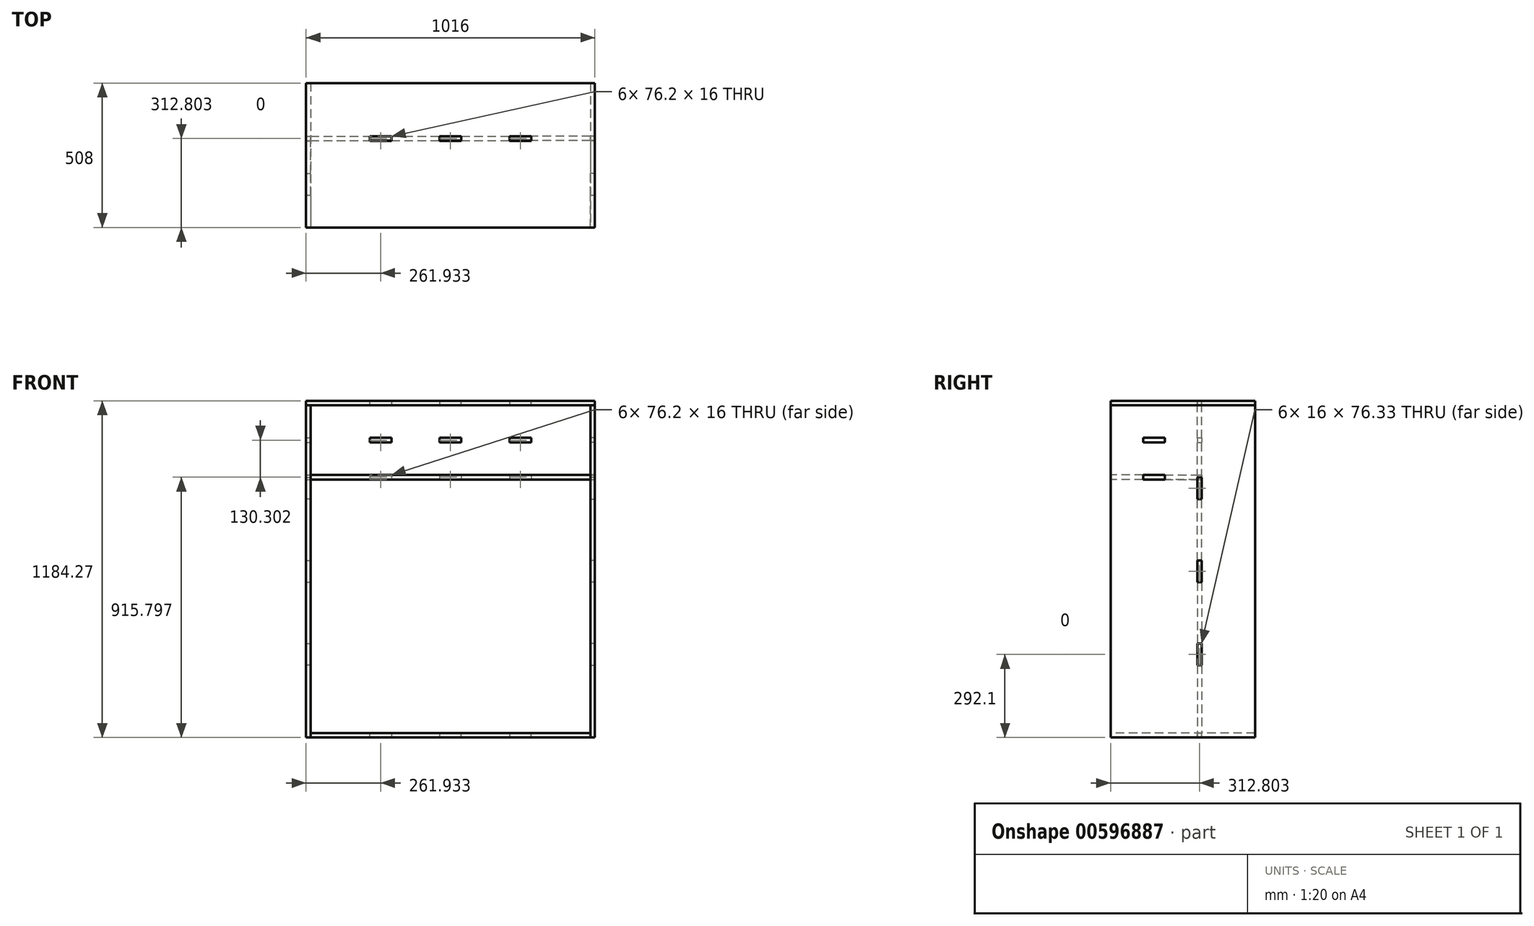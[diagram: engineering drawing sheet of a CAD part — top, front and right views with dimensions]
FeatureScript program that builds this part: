
annotation { "Feature Type Name" : "Feature", "Feature Type Description" : "" }
export const myFeature = defineFeature(function(context is Context, id is Id, definition is map)
    precondition{}
    {
        {
            var Q0;
            Q0=qCreatedBy(makeId("Top.planeOp"),FACE);
            var sketch = newSketch(context, id + "F0", { "sketchPlane" : qUnion([Q0])});
            skLineSegment(sketch, "E0.bottom", {"start": v(-880.8, 468.9) * mm, "end": v(103.44, 468.9) * mm});
            skLineSegment(sketch, "E0.top", {"start": v(-880.8, -39.1) * mm, "end": v(103.44, -39.1) * mm});
            skLineSegment(sketch, "E0.left", {"start": v(-880.8, 468.9) * mm, "end": v(-880.8, -39.1) * mm});
            skLineSegment(sketch, "E0.right", {"start": v(103.44, 468.9) * mm, "end": v(103.44, -39.1) * mm});
            skLineSegment(sketch, "E1", {"start": v(-880.8, 265.7) * mm, "end": v(103.44, 265.7) * mm, "construction": true});
            skLineSegment(sketch, "E2", {"start": v(-388.68, 468.9) * mm, "end": v(-388.68, -39.1) * mm, "construction": true});
            skPoint(sketch, "E3", {"position": v(-634.75, 468.9) * mm});
            skPoint(sketch, "E4", {"position": v(-142.62, 468.9) * mm});
            skLineSegment(sketch, "E5", {"start": v(-634.75, 468.9) * mm, "end": v(-634.75, -39.1) * mm, "construction": true});
            skLineSegment(sketch, "E6", {"start": v(-142.62, 468.9) * mm, "end": v(-142.62, -39.1) * mm, "construction": true});
            skLineSegment(sketch, "E7.bottom", {"start": v(-672.85, 265.7) * mm, "end": v(-596.65, 265.7) * mm});
            skLineSegment(sketch, "E7.top", {"start": v(-672.85, 281.7) * mm, "end": v(-596.65, 281.7) * mm});
            skLineSegment(sketch, "E7.left", {"start": v(-672.85, 265.7) * mm, "end": v(-672.85, 281.7) * mm});
            skLineSegment(sketch, "E7.right", {"start": v(-596.65, 265.7) * mm, "end": v(-596.65, 281.7) * mm});
            skPoint(sketch, "E8", {"position": v(-634.75, 281.7) * mm});
            skLineSegment(sketch, "E9.bottom", {"start": v(-426.78, 265.7) * mm, "end": v(-350.58, 265.7) * mm});
            skLineSegment(sketch, "E9.top", {"start": v(-426.78, 281.7) * mm, "end": v(-350.58, 281.7) * mm});
            skLineSegment(sketch, "E9.left", {"start": v(-426.78, 265.7) * mm, "end": v(-426.78, 281.7) * mm});
            skLineSegment(sketch, "E9.right", {"start": v(-350.58, 265.7) * mm, "end": v(-350.58, 281.7) * mm});
            skLineSegment(sketch, "E10.bottom", {"start": v(-180.72, 265.7) * mm, "end": v(-104.52, 265.7) * mm});
            skLineSegment(sketch, "E10.top", {"start": v(-180.72, 281.7) * mm, "end": v(-104.52, 281.7) * mm});
            skLineSegment(sketch, "E10.left", {"start": v(-180.72, 265.7) * mm, "end": v(-180.72, 281.7) * mm});
            skLineSegment(sketch, "E10.right", {"start": v(-104.52, 265.7) * mm, "end": v(-104.52, 281.7) * mm});
            skPoint(sketch, "E11", {"position": v(-388.68, 281.7) * mm});
            skPoint(sketch, "E12", {"position": v(-142.62, 281.7) * mm});
            skSolve(sketch);
        }
        {
            var Q0;
            Q0=makeQuery(id+"F0.imprint","IMPRINT",FACE,{"disambiguationData":[TD([[makeQuery(id+"F0.imprint","IMPRINT",EDGE,{"derivedFrom":sQuery(id+"F0.wireOp",EDGE,"E0.bottom")}),-1.0]])]});
            extrude(context, id + "F1", {"entities" : qUnion([Q0]), "depth" : 15.88 * mm, "offsetDistance" : 25.4 * mm});
        }
        {
            var Q0;
            Q0=makeQuery(id+"F1.opExtrude","SWEPT_FACE",FACE,{"disambiguationData":[OSD([sQuery(id+"F0.wireOp",EDGE,"E0.left")])]});
            var sketch = newSketch(context, id + "F2", { "sketchPlane" : qUnion([Q0])});
            skLineSegment(sketch, "E13.bottom", {"start": v(-468.9, 0) * mm, "end": v(39.1, 0) * mm});
            skLineSegment(sketch, "E13.top", {"start": v(-468.9, 1168.4) * mm, "end": v(39.1, 1168.4) * mm});
            skLineSegment(sketch, "E13.left", {"start": v(-468.9, 0) * mm, "end": v(-468.9, 1168.4) * mm});
            skLineSegment(sketch, "E13.right", {"start": v(39.1, 0) * mm, "end": v(39.1, 1168.4) * mm});
            skLineSegment(sketch, "E14", {"start": v(-468.9, 584.2) * mm, "end": v(39.1, 584.2) * mm, "construction": true});
            skLineSegment(sketch, "E15", {"start": v(-468.9, 876.3) * mm, "end": v(39.1, 876.3) * mm, "construction": true});
            skLineSegment(sketch, "E16", {"start": v(-468.9, 292.1) * mm, "end": v(39.1, 292.1) * mm, "construction": true});
            skLineSegment(sketch, "E17", {"start": v(-265.7, 1168.4) * mm, "end": v(-265.7, 0) * mm, "construction": true});
            skLineSegment(sketch, "E18.bottom", {"start": v(-265.7, 914.46) * mm, "end": v(-281.7, 914.46) * mm});
            skLineSegment(sketch, "E18.top", {"start": v(-265.7, 838.14) * mm, "end": v(-281.7, 838.14) * mm});
            skLineSegment(sketch, "E18.left", {"start": v(-265.7, 914.46) * mm, "end": v(-265.7, 838.14) * mm});
            skLineSegment(sketch, "E18.right", {"start": v(-281.7, 914.46) * mm, "end": v(-281.7, 838.14) * mm});
            skLineSegment(sketch, "E19.bottom", {"start": v(-265.7, 622.36) * mm, "end": v(-281.7, 622.36) * mm});
            skLineSegment(sketch, "E19.top", {"start": v(-265.7, 546.04) * mm, "end": v(-281.7, 546.04) * mm});
            skLineSegment(sketch, "E19.left", {"start": v(-265.7, 622.36) * mm, "end": v(-265.7, 546.04) * mm});
            skLineSegment(sketch, "E19.right", {"start": v(-281.7, 622.36) * mm, "end": v(-281.7, 546.04) * mm});
            skLineSegment(sketch, "E20.bottom", {"start": v(-265.7, 253.94) * mm, "end": v(-281.7, 253.94) * mm});
            skLineSegment(sketch, "E20.top", {"start": v(-265.7, 330.26) * mm, "end": v(-281.7, 330.26) * mm});
            skLineSegment(sketch, "E20.left", {"start": v(-265.7, 253.94) * mm, "end": v(-265.7, 330.26) * mm});
            skLineSegment(sketch, "E20.right", {"start": v(-281.7, 253.94) * mm, "end": v(-281.7, 330.26) * mm});
            skPoint(sketch, "E21", {"position": v(-281.7, 876.3) * mm});
            skPoint(sketch, "E22", {"position": v(-281.7, 584.2) * mm});
            skPoint(sketch, "E23", {"position": v(-281.7, 292.1) * mm});
            skLineSegment(sketch, "E24", {"start": v(39.1, 1054.1) * mm, "end": v(-468.9, 1054.1) * mm, "construction": true});
            skLineSegment(sketch, "E25", {"start": v(-113.3, 1168.4) * mm, "end": v(-113.3, 1054.1) * mm, "construction": true});
            skLineSegment(sketch, "E26.bottom", {"start": v(-75.14, 1054.1) * mm, "end": v(-151.46, 1054.1) * mm});
            skLineSegment(sketch, "E26.top", {"start": v(-75.14, 1038.1) * mm, "end": v(-151.46, 1038.1) * mm});
            skLineSegment(sketch, "E26.left", {"start": v(-75.14, 1054.1) * mm, "end": v(-75.14, 1038.1) * mm});
            skLineSegment(sketch, "E26.right", {"start": v(-151.46, 1054.1) * mm, "end": v(-151.46, 1038.1) * mm});
            skPoint(sketch, "E27", {"position": v(-113.3, 1054.1) * mm});
            skLineSegment(sketch, "E28", {"start": v(39.1, 923.8) * mm, "end": v(-265.7, 923.8) * mm, "construction": true});
            skPoint(sketch, "E29.oppositeSnap0", {"position": v(-151.46, 1046.1) * mm});
            skLineSegment(sketch, "E29.bottom", {"start": v(-75.14, 923.8) * mm, "end": v(-151.46, 923.8) * mm});
            skLineSegment(sketch, "E29.top", {"start": v(-75.14, 907.8) * mm, "end": v(-151.46, 907.8) * mm});
            skLineSegment(sketch, "E29.left", {"start": v(-75.14, 923.8) * mm, "end": v(-75.14, 907.8) * mm});
            skLineSegment(sketch, "E29.right", {"start": v(-151.46, 923.8) * mm, "end": v(-151.46, 907.8) * mm});
            skSolve(sketch);
        }
        {
            var Q0;
            {var subQ0=sQuery(id+"F2.wireOp",EDGE,"E13.top");Q0=makeQuery(id+"F2.imprint","IMPRINT",FACE,{"disambiguationData":[TD([[makeQuery(id+"F2.imprint","IMPRINT",EDGE,{"derivedFrom":subQ0}),-1.0]])]});}
            var Q1;
            {var subQ0=sQuery(id+"F2.wireOp",EDGE,"E13.bottom");Q1=makeQuery(id+"F2.imprint","IMPRINT",FACE,{"disambiguationData":[TD([[makeQuery(id+"F2.imprint","IMPRINT",EDGE,{"derivedFrom":subQ0}),1.0]])]});}
            extrude(context, id + "F3", {"entities" : qUnion([Q0, Q1]), "depth" : 15.88 * mm, "offsetDistance" : 25.4 * mm});
        }
        {
            var Q0;
            Q0=makeQuery(id+"F1.opExtrude","CAP_EDGE",EDGE,{"disambiguationData":[OSD([sQuery(id+"F0.wireOp",EDGE,"E0.top")])],"isStart":false});
            cPoint(context, id + "F4", {"entities" : qUnion([Q0]), "parameter" : 0.5});
        }
        {
            var Q0;
            Q0=makeQuery(id+"F1.opExtrude","CAP_EDGE",EDGE,{"disambiguationData":[OSD([sQuery(id+"F0.wireOp",EDGE,"E0.bottom")])],"isStart":false});
            cPoint(context, id + "F5", {"entities" : qUnion([Q0]), "parameter" : 0.5});
        }
        {
            var Q0;
            Q0=makeQuery(id+"F1.opExtrude","CAP_EDGE",EDGE,{"disambiguationData":[OSD([sQuery(id+"F0.wireOp",EDGE,"E0.top")])],"isStart":true});
            cPoint(context, id + "F6", {"entities" : qUnion([Q0]), "parameter" : 0.5});
        }
        {
            var Q0;
            Q0 = qCreatedBy(id + "F4" ,VERTEX);
            var Q1;
            Q1 = qCreatedBy(id + "F5" ,VERTEX);
            var Q2;
            Q2 = qCreatedBy(id + "F6" ,VERTEX);
            cPlane(context, id + "F7", {"entities" : qUnion([Q0, Q1, Q2]), "cplaneType" : CPlaneType.THREE_POINT, "offset" : 25.4 * mm, "width" : 152.4 * mm, "height" : 152.4 * mm});
        }
        {
            var Q0;
            Q0=makeQuery(id+"F3.opExtrude","SWEPT_BODY",BODY,{"disambiguationData":[OSD([sQuery(id+"F2.wireOp",EDGE,"E13.bottom"),sQuery(id+"F2.wireOp",EDGE,"E13.top"),sQuery(id+"F2.wireOp",EDGE,"E13.left"),sQuery(id+"F2.wireOp",EDGE,"E13.right"),sQuery(id+"F2.wireOp",EDGE,"E18.bottom"),sQuery(id+"F2.wireOp",EDGE,"E18.top"),sQuery(id+"F2.wireOp",EDGE,"E18.left"),sQuery(id+"F2.wireOp",EDGE,"E18.right"),sQuery(id+"F2.wireOp",EDGE,"E19.bottom"),sQuery(id+"F2.wireOp",EDGE,"E19.top"),sQuery(id+"F2.wireOp",EDGE,"E19.left"),sQuery(id+"F2.wireOp",EDGE,"E19.right"),sQuery(id+"F2.wireOp",EDGE,"E20.bottom"),sQuery(id+"F2.wireOp",EDGE,"E20.top"),sQuery(id+"F2.wireOp",EDGE,"E20.left"),sQuery(id+"F2.wireOp",EDGE,"E20.right")])]});
            var Q1;
            Q1=qCreatedBy(id+"F7.planeOp",FACE);
            mirror(context, id + "F8", {"entities" : qUnion([Q0]), "mirrorPlane" : qUnion([Q1])});
        }
        {
            var Q0;
            Q0=makeQuery(id+"F3.opExtrude","SWEPT_FACE",FACE,{"disambiguationData":[OSD([sQuery(id+"F2.wireOp",EDGE,"E13.top")])]});
            var sketch = newSketch(context, id + "F9", { "sketchPlane" : qUnion([Q0])});
            skLineSegment(sketch, "E30.bottom", {"start": v(-896.68, 468.9) * mm, "end": v(119.32, 468.9) * mm});
            skLineSegment(sketch, "E30.top", {"start": v(-896.68, -39.1) * mm, "end": v(119.32, -39.1) * mm});
            skLineSegment(sketch, "E30.left", {"start": v(-896.68, 468.9) * mm, "end": v(-896.68, -39.1) * mm});
            skLineSegment(sketch, "E30.right", {"start": v(119.32, 468.9) * mm, "end": v(119.32, -39.1) * mm});
            skLineSegment(sketch, "E31.bottom", {"start": v(-672.85, 265.7) * mm, "end": v(-596.65, 265.7) * mm});
            skLineSegment(sketch, "E31.top", {"start": v(-672.85, 281.7) * mm, "end": v(-596.65, 281.7) * mm});
            skLineSegment(sketch, "E31.left", {"start": v(-672.85, 265.7) * mm, "end": v(-672.85, 281.7) * mm});
            skLineSegment(sketch, "E31.right", {"start": v(-596.65, 265.7) * mm, "end": v(-596.65, 281.7) * mm});
            skLineSegment(sketch, "E32.bottom", {"start": v(-426.78, 265.7) * mm, "end": v(-350.58, 265.7) * mm});
            skLineSegment(sketch, "E32.top", {"start": v(-426.78, 281.7) * mm, "end": v(-350.58, 281.7) * mm});
            skLineSegment(sketch, "E32.left", {"start": v(-426.78, 265.7) * mm, "end": v(-426.78, 281.7) * mm});
            skLineSegment(sketch, "E32.right", {"start": v(-350.58, 265.7) * mm, "end": v(-350.58, 281.7) * mm});
            skPoint(sketch, "E33", {"position": v(-634.75, 281.7) * mm});
            skPoint(sketch, "E34", {"position": v(-388.68, 281.7) * mm});
            skLineSegment(sketch, "E35", {"start": v(-388.68, 468.9) * mm, "end": v(-388.68, -39.1) * mm, "construction": true});
            skLineSegment(sketch, "E36", {"start": v(-634.75, 468.9) * mm, "end": v(-634.75, -39.1) * mm, "construction": true});
            skPoint(sketch, "E37", {"position": v(-880.8, 468.9) * mm});
            skLineSegment(sketch, "E38.MirrorCS", {"start": v(-672.85, 297.7) * mm, "end": v(-672.85, 281.7) * mm});
            skLineSegment(sketch, "E39.MirrorCS", {"start": v(-104.52, 265.7) * mm, "end": v(-104.52, 281.7) * mm});
            skLineSegment(sketch, "E40.MirrorCS", {"start": v(-104.52, 281.7) * mm, "end": v(-180.72, 281.7) * mm});
            skLineSegment(sketch, "E41.MirrorCS", {"start": v(-180.72, 265.7) * mm, "end": v(-180.72, 281.7) * mm});
            skLineSegment(sketch, "E42.MirrorCS", {"start": v(119.32, 265.7) * mm, "end": v(-896.68, 265.7) * mm, "construction": true});
            skLineSegment(sketch, "E43", {"start": v(-180.72, 265.7) * mm, "end": v(-104.52, 265.7) * mm});
            skSolve(sketch);
        }
        {
            var Q0;
            {var subQ2=sQuery(id+"F9.wireOp",EDGE,"E30.right");Q0=makeQuery(id+"F9.imprint","IMPRINT",FACE,{"disambiguationData":[TD([[makeQuery(id+"F9.imprint","IMPRINT",EDGE,{"derivedFrom":subQ2}),-1.0]])]});}
            var Q1;
            {var subQ2=sQuery(id+"F9.wireOp",EDGE,"E30.left");Q1=makeQuery(id+"F9.imprint","IMPRINT",FACE,{"disambiguationData":[TD([[makeQuery(id+"F9.imprint","IMPRINT",EDGE,{"derivedFrom":subQ2}),1.0]])]});}
            extrude(context, id + "F10", {"entities" : qUnion([Q0, Q1]), "depth" : 15.88 * mm, "offsetDistance" : 25.4 * mm});
        }
        {
            var Q0;
            Q0=makeQuery(id+"F8.opPattern","COPY",FACE,{"derivedFrom":makeQuery(id+"F3.opExtrude","SWEPT_FACE",FACE,{"disambiguationData":[OSD([sQuery(id+"F2.wireOp",EDGE,"E19.right")])]}),"instanceName":"1"});
            var sketch = newSketch(context, id + "F11", { "sketchPlane" : qUnion([Q0])});
            skLineSegment(sketch, "E44.0.1", {"start": v(-350.58, 1168.4) * mm, "end": v(-350.58, 1184.28) * mm});
            skLineSegment(sketch, "E44.0.2", {"start": v(-350.58, 1184.28) * mm, "end": v(-426.78, 1184.28) * mm});
            skLineSegment(sketch, "E44.0.3", {"start": v(-426.78, 1184.28) * mm, "end": v(-426.78, 1168.4) * mm});
            skLineSegment(sketch, "E45.0.1", {"start": v(-104.52, 1168.4) * mm, "end": v(-104.52, 1184.28) * mm});
            skLineSegment(sketch, "E45.0.2", {"start": v(-104.52, 1184.28) * mm, "end": v(-180.72, 1184.28) * mm});
            skLineSegment(sketch, "E45.0.3", {"start": v(-180.72, 1184.28) * mm, "end": v(-180.72, 1168.4) * mm});
            skLineSegment(sketch, "E46.0.0", {"start": v(-426.78, 0) * mm, "end": v(-350.58, 0) * mm});
            skLineSegment(sketch, "E46.0.1", {"start": v(-350.58, 0) * mm, "end": v(-350.58, 15.88) * mm});
            skLineSegment(sketch, "E46.0.3", {"start": v(-426.78, 15.88) * mm, "end": v(-426.78, 0) * mm});
            skLineSegment(sketch, "E47.0.0", {"start": v(-180.72, 0) * mm, "end": v(-104.52, 0) * mm});
            skLineSegment(sketch, "E47.0.1", {"start": v(-104.52, 0) * mm, "end": v(-104.52, 15.88) * mm});
            skLineSegment(sketch, "E47.0.3", {"start": v(-180.72, 15.88) * mm, "end": v(-180.72, 0) * mm});
            skLineSegment(sketch, "E48.0.1", {"start": v(103.44, 253.94) * mm, "end": v(119.32, 253.94) * mm});
            skLineSegment(sketch, "E48.0.2", {"start": v(119.32, 253.94) * mm, "end": v(119.32, 330.26) * mm});
            skLineSegment(sketch, "E48.0.3", {"start": v(119.32, 330.26) * mm, "end": v(103.44, 330.26) * mm});
            skLineSegment(sketch, "E49.0.1", {"start": v(103.44, 838.14) * mm, "end": v(119.32, 838.14) * mm});
            skLineSegment(sketch, "E49.0.2", {"start": v(119.32, 838.14) * mm, "end": v(119.32, 914.46) * mm});
            skLineSegment(sketch, "E49.0.3", {"start": v(119.32, 914.46) * mm, "end": v(103.44, 914.46) * mm});
            skLineSegment(sketch, "E50", {"start": v(-388.68, 1168.4) * mm, "end": v(-388.68, 15.88) * mm, "construction": true});
            skLineSegment(sketch, "E51", {"start": v(-350.58, 1168.4) * mm, "end": v(-180.72, 1168.4) * mm});
            skLineSegment(sketch, "E52", {"start": v(119.32, 622.36) * mm, "end": v(103.44, 622.36) * mm});
            skLineSegment(sketch, "E53", {"start": v(103.44, 622.36) * mm, "end": v(103.44, 838.14) * mm});
            skLineSegment(sketch, "E54", {"start": v(119.32, 622.36) * mm, "end": v(119.32, 546.04) * mm});
            skLineSegment(sketch, "E55", {"start": v(119.32, 546.04) * mm, "end": v(103.44, 546.04) * mm});
            skLineSegment(sketch, "E56", {"start": v(103.44, 546.04) * mm, "end": v(103.44, 330.26) * mm});
            skLineSegment(sketch, "E57", {"start": v(103.44, 253.94) * mm, "end": v(103.44, 15.88) * mm});
            skLineSegment(sketch, "E58", {"start": v(103.44, 15.88) * mm, "end": v(-104.52, 15.88) * mm});
            skLineSegment(sketch, "E59", {"start": v(-180.72, 15.88) * mm, "end": v(-350.58, 15.88) * mm});
            skLineSegment(sketch, "E60", {"start": v(103.44, 914.46) * mm, "end": v(103.44, 1168.4) * mm});
            skLineSegment(sketch, "E61", {"start": v(103.44, 1168.4) * mm, "end": v(-104.52, 1168.4) * mm});
            skLineSegment(sketch, "E62", {"start": v(-180.72, 1168.4) * mm, "end": v(-350.58, 1168.4) * mm});
            skLineSegment(sketch, "E63.MirrorCS", {"start": v(-596.65, 1184.28) * mm, "end": v(-596.65, 1168.4) * mm});
            skLineSegment(sketch, "E64.MirrorCS", {"start": v(-896.68, 914.46) * mm, "end": v(-880.8, 914.46) * mm});
            skLineSegment(sketch, "E65.MirrorCS", {"start": v(-896.68, 622.36) * mm, "end": v(-880.8, 622.36) * mm});
            skLineSegment(sketch, "E66.MirrorCS", {"start": v(-880.8, 838.14) * mm, "end": v(-896.68, 838.14) * mm});
            skLineSegment(sketch, "E67.MirrorCS", {"start": v(-672.85, 1168.4) * mm, "end": v(-672.85, 1184.28) * mm});
            skLineSegment(sketch, "E68.MirrorCS", {"start": v(-672.85, 0) * mm, "end": v(-672.85, 15.88) * mm});
            skLineSegment(sketch, "E69.MirrorCS", {"start": v(-880.8, 253.94) * mm, "end": v(-896.68, 253.94) * mm});
            skLineSegment(sketch, "E70.MirrorCS", {"start": v(-596.65, 15.88) * mm, "end": v(-596.65, 0) * mm});
            skLineSegment(sketch, "E71.MirrorCS", {"start": v(-896.68, 546.04) * mm, "end": v(-880.8, 546.04) * mm});
            skLineSegment(sketch, "E72.MirrorCS", {"start": v(-896.68, 330.26) * mm, "end": v(-880.8, 330.26) * mm});
            skLineSegment(sketch, "E73.MirrorCS", {"start": v(-880.8, 622.36) * mm, "end": v(-880.8, 838.14) * mm});
            skLineSegment(sketch, "E74.MirrorCS", {"start": v(-896.68, 253.94) * mm, "end": v(-896.68, 330.26) * mm});
            skLineSegment(sketch, "E75.MirrorCS", {"start": v(-880.8, 15.88) * mm, "end": v(-672.85, 15.88) * mm});
            skLineSegment(sketch, "E76.MirrorCS", {"start": v(-880.8, 1168.4) * mm, "end": v(-672.85, 1168.4) * mm});
            skLineSegment(sketch, "E77.MirrorCS", {"start": v(-880.8, 914.46) * mm, "end": v(-880.8, 1168.4) * mm});
            skLineSegment(sketch, "E78.MirrorCS", {"start": v(-672.85, 1184.28) * mm, "end": v(-596.65, 1184.28) * mm});
            skLineSegment(sketch, "E79.MirrorCS", {"start": v(-596.65, 0) * mm, "end": v(-672.85, 0) * mm});
            skLineSegment(sketch, "E80.MirrorCS", {"start": v(-896.68, 622.36) * mm, "end": v(-896.68, 546.04) * mm});
            skLineSegment(sketch, "E81.MirrorCS", {"start": v(-880.8, 546.04) * mm, "end": v(-880.8, 330.26) * mm});
            skLineSegment(sketch, "E82.MirrorCS", {"start": v(-896.68, 838.14) * mm, "end": v(-896.68, 914.46) * mm});
            skLineSegment(sketch, "E83.MirrorCS", {"start": v(-880.8, 253.94) * mm, "end": v(-880.8, 15.88) * mm});
            skLineSegment(sketch, "E84.MirrorCS", {"start": v(-596.65, 15.88) * mm, "end": v(-426.78, 15.88) * mm});
            skLineSegment(sketch, "E85.MirrorCS", {"start": v(-596.65, 1168.4) * mm, "end": v(-426.78, 1168.4) * mm});
            skLineSegment(sketch, "E86", {"start": v(-880.8, 1054.1) * mm, "end": v(103.44, 1054.1) * mm, "construction": true});
            skPoint(sketch, "E86.endSnap0", {"position": v(103.44, 1041.43) * mm});
            skLineSegment(sketch, "E87.bottom", {"start": v(-426.78, 1054.1) * mm, "end": v(-350.58, 1054.1) * mm});
            skLineSegment(sketch, "E87.top", {"start": v(-426.78, 1038.1) * mm, "end": v(-350.58, 1038.1) * mm});
            skLineSegment(sketch, "E87.left", {"start": v(-426.78, 1054.1) * mm, "end": v(-426.78, 1038.1) * mm});
            skLineSegment(sketch, "E87.right", {"start": v(-350.58, 1054.1) * mm, "end": v(-350.58, 1038.1) * mm});
            skLineSegment(sketch, "E88.bottom", {"start": v(-180.72, 1054.1) * mm, "end": v(-104.52, 1054.1) * mm});
            skLineSegment(sketch, "E88.top", {"start": v(-180.72, 1038.1) * mm, "end": v(-104.52, 1038.1) * mm});
            skLineSegment(sketch, "E88.left", {"start": v(-180.72, 1054.1) * mm, "end": v(-180.72, 1038.1) * mm});
            skLineSegment(sketch, "E88.right", {"start": v(-104.52, 1054.1) * mm, "end": v(-104.52, 1038.1) * mm});
            skLineSegment(sketch, "E89.bottom", {"start": v(-596.65, 1054.1) * mm, "end": v(-672.85, 1054.1) * mm});
            skLineSegment(sketch, "E89.top", {"start": v(-596.65, 1038.1) * mm, "end": v(-672.85, 1038.1) * mm});
            skLineSegment(sketch, "E89.left", {"start": v(-596.65, 1054.1) * mm, "end": v(-596.65, 1038.1) * mm});
            skLineSegment(sketch, "E89.right", {"start": v(-672.85, 1054.1) * mm, "end": v(-672.85, 1038.1) * mm});
            skLineSegment(sketch, "E90", {"start": v(-880.8, 923.8) * mm, "end": v(103.44, 923.8) * mm, "construction": true});
            skLineSegment(sketch, "E91.bottom", {"start": v(-672.85, 923.8) * mm, "end": v(-596.65, 923.8) * mm});
            skLineSegment(sketch, "E91.top", {"start": v(-672.85, 907.8) * mm, "end": v(-596.65, 907.8) * mm});
            skLineSegment(sketch, "E91.left", {"start": v(-672.85, 923.8) * mm, "end": v(-672.85, 907.8) * mm});
            skLineSegment(sketch, "E91.right", {"start": v(-596.65, 923.8) * mm, "end": v(-596.65, 907.8) * mm});
            skLineSegment(sketch, "E92.bottom", {"start": v(-426.78, 923.8) * mm, "end": v(-350.58, 923.8) * mm});
            skLineSegment(sketch, "E92.top", {"start": v(-426.78, 907.8) * mm, "end": v(-350.58, 907.8) * mm});
            skLineSegment(sketch, "E92.left", {"start": v(-426.78, 923.8) * mm, "end": v(-426.78, 907.8) * mm});
            skLineSegment(sketch, "E92.right", {"start": v(-350.58, 923.8) * mm, "end": v(-350.58, 907.8) * mm});
            skLineSegment(sketch, "E93.bottom", {"start": v(-180.72, 923.8) * mm, "end": v(-104.52, 923.8) * mm});
            skLineSegment(sketch, "E93.top", {"start": v(-180.72, 907.8) * mm, "end": v(-104.52, 907.8) * mm});
            skLineSegment(sketch, "E93.left", {"start": v(-180.72, 923.8) * mm, "end": v(-180.72, 907.8) * mm});
            skLineSegment(sketch, "E93.right", {"start": v(-104.52, 923.8) * mm, "end": v(-104.52, 907.8) * mm});
            skSolve(sketch);
        }
        {
            var Q0;
            Q0=makeQuery(id+"F11.imprint","IMPRINT",FACE,{"disambiguationData":[TD([[makeQuery(id+"F11.imprint","IMPRINT",EDGE,{"derivedFrom":sQuery(id+"F11.wireOp",EDGE,"E44.0.1")}),1.0]])]});
            var Q1;
            Q1=makeQuery(id+"F11.imprint","IMPRINT",FACE,{"disambiguationData":[TD([[makeQuery(id+"F11.imprint","IMPRINT",EDGE,{"derivedFrom":sQuery(id+"F11.wireOp",EDGE,"E52")}),1.0]])]});
            extrude(context, id + "F12", {"entities" : qUnion([Q0, Q1]), "depth" : 15.88 * mm, "offsetDistance" : 25.4 * mm});
        }
        {
            var Q0;
            Q0=makeQuery(id+"F3.opExtrude","SWEPT_FACE",FACE,{"disambiguationData":[OSD([sQuery(id+"F2.wireOp",EDGE,"E29.top")])]});
            var sketch = newSketch(context, id + "F13", { "sketchPlane" : qUnion([Q0])});
            skLineSegment(sketch, "E94.0.0", {"start": v(-596.65, 281.7) * mm, "end": v(-672.85, 281.7) * mm});
            skLineSegment(sketch, "E94.0.1", {"start": v(-672.85, 281.7) * mm, "end": v(-672.85, 265.83) * mm});
            skLineSegment(sketch, "E94.0.3", {"start": v(-596.65, 265.83) * mm, "end": v(-596.65, 281.7) * mm});
            skLineSegment(sketch, "E95.0.0", {"start": v(-350.58, 281.7) * mm, "end": v(-426.78, 281.7) * mm});
            skLineSegment(sketch, "E95.0.1", {"start": v(-426.78, 281.7) * mm, "end": v(-426.78, 265.83) * mm});
            skLineSegment(sketch, "E95.0.3", {"start": v(-350.58, 265.83) * mm, "end": v(-350.58, 281.7) * mm});
            skLineSegment(sketch, "E96.0.0", {"start": v(-104.52, 281.7) * mm, "end": v(-180.72, 281.7) * mm});
            skLineSegment(sketch, "E96.0.1", {"start": v(-180.72, 281.7) * mm, "end": v(-180.72, 265.83) * mm});
            skLineSegment(sketch, "E96.0.3", {"start": v(-104.52, 265.83) * mm, "end": v(-104.52, 281.7) * mm});
            skLineSegment(sketch, "E97.0.1", {"start": v(103.44, 75.14) * mm, "end": v(119.32, 75.14) * mm});
            skLineSegment(sketch, "E97.0.2", {"start": v(119.32, 75.14) * mm, "end": v(119.32, 151.46) * mm});
            skLineSegment(sketch, "E97.0.3", {"start": v(119.32, 151.46) * mm, "end": v(103.44, 151.46) * mm});
            skLineSegment(sketch, "E98", {"start": v(-880.8, 75.14) * mm, "end": v(-896.68, 75.14) * mm});
            skLineSegment(sketch, "E99", {"start": v(-896.68, 75.14) * mm, "end": v(-896.68, 151.46) * mm});
            skLineSegment(sketch, "E100", {"start": v(-896.68, 151.46) * mm, "end": v(-880.8, 151.46) * mm});
            skLineSegment(sketch, "E101", {"start": v(-880.8, 151.46) * mm, "end": v(-880.8, 265.83) * mm});
            skLineSegment(sketch, "E102", {"start": v(-880.8, 265.83) * mm, "end": v(-672.85, 265.83) * mm});
            skLineSegment(sketch, "E103", {"start": v(-596.65, 265.83) * mm, "end": v(-426.78, 265.83) * mm});
            skLineSegment(sketch, "E104", {"start": v(-350.58, 265.83) * mm, "end": v(-180.72, 265.83) * mm});
            skLineSegment(sketch, "E105", {"start": v(-104.52, 265.83) * mm, "end": v(103.44, 265.83) * mm});
            skLineSegment(sketch, "E106", {"start": v(103.44, 265.83) * mm, "end": v(103.44, 151.46) * mm});
            skLineSegment(sketch, "E107.0", {"start": v(-880.8, -39.1) * mm, "end": v(103.44, -39.1) * mm});
            skLineSegment(sketch, "E108", {"start": v(-880.8, 75.14) * mm, "end": v(-880.8, -39.1) * mm});
            skLineSegment(sketch, "E109", {"start": v(103.44, -39.1) * mm, "end": v(103.44, 75.14) * mm});
            skSolve(sketch);
        }
        {
            var Q0;
            Q0=makeQuery(id+"F13.imprint","IMPRINT",FACE,{"disambiguationData":[TD([[makeQuery(id+"F13.imprint","IMPRINT",EDGE,{"derivedFrom":sQuery(id+"F13.wireOp",EDGE,"E94.0.0")}),1.0]])]});
            var Q1;
            Q1=makeQuery(id+"F13.imprint","IMPRINT",FACE,{"disambiguationData":[TD([[makeQuery(id+"F13.imprint","IMPRINT",EDGE,{"derivedFrom":sQuery(id+"F13.wireOp",EDGE,"E98")}),1.0]])]});
            extrude(context, id + "F14", {"entities" : qUnion([Q0, Q1]), "depth" : 15.88 * mm, "offsetDistance" : 25.4 * mm});
        }
    });
